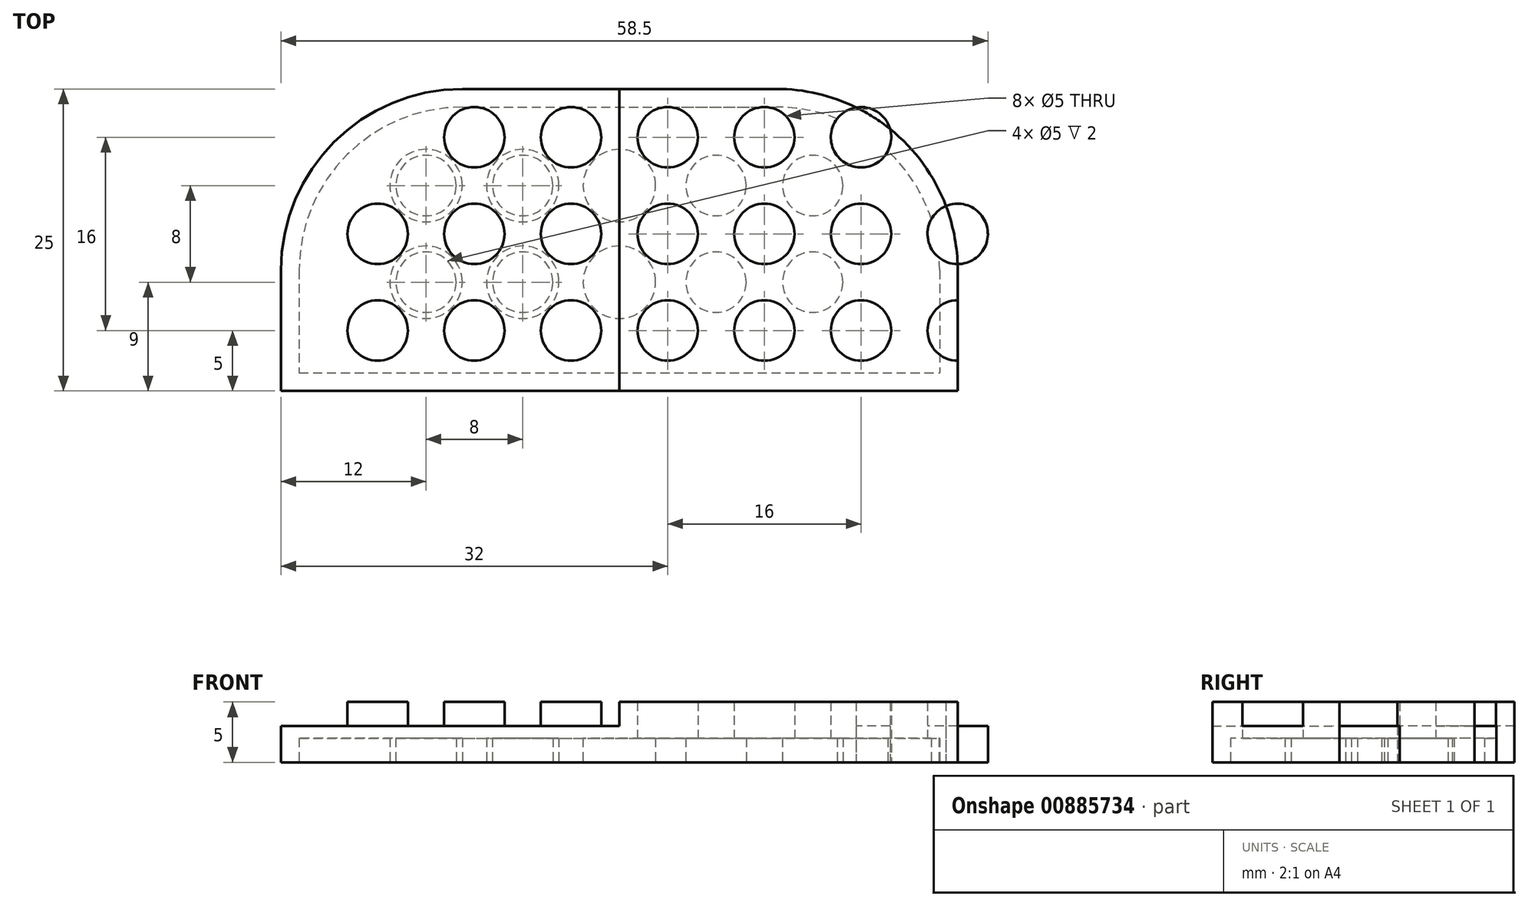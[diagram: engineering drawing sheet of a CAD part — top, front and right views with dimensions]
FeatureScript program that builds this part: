
annotation { "Feature Type Name" : "Feature", "Feature Type Description" : "" }
export const myFeature = defineFeature(function(context is Context, id is Id, definition is map)
    precondition{}
    {
        {
            var Q0;
            Q0=qCreatedBy(makeId("Top.planeOp"),FACE);
            var sketch = newSketch(context, id + "F0", { "sketchPlane" : qUnion([Q0])});
            skLineSegment(sketch, "E0.bottom", {"start": v(0, 0) * mm, "end": v(-28, 0) * mm});
            skLineSegment(sketch, "E0.top", {"start": v(0, 25) * mm, "end": v(-13, 25) * mm});
            skLineSegment(sketch, "E0.left", {"start": v(0, 0) * mm, "end": v(0, 25) * mm});
            skLineSegment(sketch, "E0.right", {"start": v(-28, 0) * mm, "end": v(-28, 10) * mm});
            skPoint(sketch, "E1.visualSharp", {"position": v(-28, 25) * mm});
            skArc(sketch, "E1.filletArc", {"start": v(-13, 25) * mm, "mid": v(-23.6, 20.6) * mm, "end": v(-28, 10) * mm});
            skLineSegment(sketch, "E2.MirrorCS", {"start": v(0, 25) * mm, "end": v(13, 25) * mm});
            skArc(sketch, "E3.MirrorCS", {"start": v(13, 25) * mm, "mid": v(23.6, 20.6) * mm, "end": v(28, 10) * mm});
            skLineSegment(sketch, "E4.MirrorCS", {"start": v(28, 0) * mm, "end": v(28, 10) * mm});
            skLineSegment(sketch, "E5.MirrorCS", {"start": v(0, 0) * mm, "end": v(28, 0) * mm});
            skCircle(sketch, "E6", {"center": v(-20, 5) * mm, "radius": 2.5 * mm});
            skCircle(sketch, "E7", {"center": v(-12, 5) * mm, "radius": 2.5 * mm});
            skCircle(sketch, "E8", {"center": v(-4, 5) * mm, "radius": 2.5 * mm});
            skCircle(sketch, "E9.MirrorC", {"center": v(4, 5) * mm, "radius": 2.5 * mm});
            skCircle(sketch, "E10.MirrorC", {"center": v(12, 5) * mm, "radius": 2.5 * mm});
            skCircle(sketch, "E11.MirrorC", {"center": v(20, 5) * mm, "radius": 2.5 * mm});
            skCircle(sketch, "E12", {"center": v(-20, 13) * mm, "radius": 2.5 * mm});
            skCircle(sketch, "E13", {"center": v(-12, 13) * mm, "radius": 2.5 * mm});
            skCircle(sketch, "E14", {"center": v(-4, 13) * mm, "radius": 2.5 * mm});
            skCircle(sketch, "E15", {"center": v(-12, 21) * mm, "radius": 2.5 * mm});
            skCircle(sketch, "E16", {"center": v(-4, 21) * mm, "radius": 2.5 * mm});
            skCircle(sketch, "E17", {"center": v(-20, 21) * mm, "radius": 2.5 * mm});
            skCircle(sketch, "E18.MirrorC", {"center": v(4, 21) * mm, "radius": 2.5 * mm});
            skCircle(sketch, "E19.MirrorC", {"center": v(12, 21) * mm, "radius": 2.5 * mm});
            skCircle(sketch, "E20.MirrorC", {"center": v(20, 21) * mm, "radius": 2.5 * mm});
            skCircle(sketch, "E21.MirrorC", {"center": v(20, 13) * mm, "radius": 2.5 * mm});
            skCircle(sketch, "E22.MirrorC", {"center": v(12, 13) * mm, "radius": 2.5 * mm});
            skCircle(sketch, "E23.MirrorC", {"center": v(4, 13) * mm, "radius": 2.5 * mm});
            skCircle(sketch, "E24", {"center": v(28, 13) * mm, "radius": 2.5 * mm});
            skCircle(sketch, "E25", {"center": v(28, 5) * mm, "radius": 2.5 * mm});
            skCircle(sketch, "E26.MirrorC", {"center": v(-28, 13) * mm, "radius": 2.5 * mm});
            skCircle(sketch, "E27.MirrorC", {"center": v(-28, 5) * mm, "radius": 2.5 * mm});
            skCircle(sketch, "E28", {"center": v(-28, 21) * mm, "radius": 2.5 * mm});
            skCircle(sketch, "E29.MirrorC", {"center": v(28, 21) * mm, "radius": 2.5 * mm});
            skSolve(sketch);
        }
        {
            var Q0;
            {var subQ12=sQuery(id+"F0.wireOp",EDGE,"E0.bottom");Q0=makeQuery(id+"F0.imprint","IMPRINT",FACE,{"disambiguationData":[TD([[makeQuery(id+"F0.imprint","IMPRINT",EDGE,{"derivedFrom":subQ12}),-1.0]])]});}
            var Q1;
            {var subQ0=sQuery(id+"F0.wireOp",EDGE,"E17");var subQ1=sQuery(id+"F0.wireOp",EDGE,"E1.filletArc");var subQ2=makeQuery(id+"F0.imprint","INTERSECT",VERTEX,{"disambiguationData":[OD(0.0)],"derivedFrom":[subQ1,subQ0]});Q1=makeQuery(id+"F0.imprint","IMPRINT",FACE,{"disambiguationData":[TD([[makeQuery(id+"F0.imprint","IMPRINT",EDGE,{"disambiguationData":[TD([[subQ2,-1.0]])],"derivedFrom":subQ1}),1.0]])]});}
            var Q2;
            {var subQ10=sQuery(id+"F0.wireOp",EDGE,"E2.MirrorCS");Q2=makeQuery(id+"F0.imprint","IMPRINT",FACE,{"disambiguationData":[TD([[makeQuery(id+"F0.imprint","IMPRINT",EDGE,{"derivedFrom":subQ10}),-1.0]])]});}
            var Q3;
            {var subQ0=sQuery(id+"F0.wireOp",EDGE,"E20.MirrorC");var subQ1=sQuery(id+"F0.wireOp",EDGE,"E3.MirrorCS");var subQ2=makeQuery(id+"F0.imprint","INTERSECT",VERTEX,{"disambiguationData":[OD(0.0)],"derivedFrom":[subQ1,subQ0]});Q3=makeQuery(id+"F0.imprint","IMPRINT",FACE,{"disambiguationData":[TD([[makeQuery(id+"F0.imprint","IMPRINT",EDGE,{"disambiguationData":[TD([[subQ2,-1.0]])],"derivedFrom":subQ1}),-1.0]])]});}
            var Q4;
            {var subQ0=sQuery(id+"F0.wireOp",EDGE,"E26.MirrorC");var subQ1=sQuery(id+"F0.wireOp",EDGE,"E1.filletArc");var subQ2=makeQuery(id+"F0.imprint","INTERSECT",VERTEX,{"disambiguationData":[OD(0.0)],"derivedFrom":[subQ1,subQ0]});Q4=makeQuery(id+"F0.imprint","IMPRINT",FACE,{"disambiguationData":[TD([[makeQuery(id+"F0.imprint","IMPRINT",EDGE,{"disambiguationData":[TD([[subQ2,-1.0]])],"derivedFrom":subQ1}),1.0]])]});}
            var Q5;
            {var subQ0=sQuery(id+"F0.wireOp",EDGE,"E27.MirrorC");var subQ1=sQuery(id+"F0.wireOp",EDGE,"E0.right");var subQ2=makeQuery(id+"F0.imprint","INTERSECT",VERTEX,{"disambiguationData":[OD(0.0)],"derivedFrom":[subQ1,subQ0]});Q5=makeQuery(id+"F0.imprint","IMPRINT",FACE,{"disambiguationData":[TD([[makeQuery(id+"F0.imprint","IMPRINT",EDGE,{"disambiguationData":[TD([[subQ2,-1.0]])],"derivedFrom":subQ1}),-1.0]])]});}
            var Q6;
            {var subQ0=sQuery(id+"F0.wireOp",EDGE,"E25");var subQ1=sQuery(id+"F0.wireOp",EDGE,"E4.MirrorCS");var subQ2=makeQuery(id+"F0.imprint","INTERSECT",VERTEX,{"disambiguationData":[OD(0.0)],"derivedFrom":[subQ1,subQ0]});Q6=makeQuery(id+"F0.imprint","IMPRINT",FACE,{"disambiguationData":[TD([[makeQuery(id+"F0.imprint","IMPRINT",EDGE,{"disambiguationData":[TD([[subQ2,-1.0]])],"derivedFrom":subQ1}),1.0]])]});}
            var Q7;
            {var subQ0=sQuery(id+"F0.wireOp",EDGE,"E24");var subQ1=sQuery(id+"F0.wireOp",EDGE,"E3.MirrorCS");var subQ2=makeQuery(id+"F0.imprint","INTERSECT",VERTEX,{"disambiguationData":[OD(0.0)],"derivedFrom":[subQ1,subQ0]});Q7=makeQuery(id+"F0.imprint","IMPRINT",FACE,{"disambiguationData":[TD([[makeQuery(id+"F0.imprint","IMPRINT",EDGE,{"disambiguationData":[TD([[subQ2,-1.0]])],"derivedFrom":subQ1}),-1.0]])]});}
            extrude(context, id + "F1", {"entities" : qUnion([Q0, Q1, Q2, Q3, Q4, Q5, Q6, Q7]), "depth" : 3 * mm, "offsetDistance" : 25 * mm});
        }
        {
            var Q0;
            Q0=makeQuery(id+"F0.imprint","IMPRINT",FACE,{"disambiguationData":[TD([[makeQuery(id+"F0.imprint","IMPRINT",EDGE,{"derivedFrom":sQuery(id+"F0.wireOp",EDGE,"E12")}),1.0]])]});
            var Q1;
            Q1=makeQuery(id+"F0.imprint","IMPRINT",FACE,{"disambiguationData":[TD([[makeQuery(id+"F0.imprint","IMPRINT",EDGE,{"derivedFrom":sQuery(id+"F0.wireOp",EDGE,"E6")}),1.0]])]});
            var Q2;
            Q2=makeQuery(id+"F0.imprint","IMPRINT",FACE,{"disambiguationData":[TD([[makeQuery(id+"F0.imprint","IMPRINT",EDGE,{"derivedFrom":sQuery(id+"F0.wireOp",EDGE,"E7")}),1.0]])]});
            var Q3;
            Q3=makeQuery(id+"F0.imprint","IMPRINT",FACE,{"disambiguationData":[TD([[makeQuery(id+"F0.imprint","IMPRINT",EDGE,{"derivedFrom":sQuery(id+"F0.wireOp",EDGE,"E13")}),1.0]])]});
            var Q4;
            Q4=makeQuery(id+"F0.imprint","IMPRINT",FACE,{"disambiguationData":[TD([[makeQuery(id+"F0.imprint","IMPRINT",EDGE,{"derivedFrom":sQuery(id+"F0.wireOp",EDGE,"E15")}),1.0]])]});
            var Q5;
            Q5=makeQuery(id+"F0.imprint","IMPRINT",FACE,{"disambiguationData":[TD([[makeQuery(id+"F0.imprint","IMPRINT",EDGE,{"derivedFrom":sQuery(id+"F0.wireOp",EDGE,"E16")}),1.0]])]});
            var Q6;
            Q6=makeQuery(id+"F0.imprint","IMPRINT",FACE,{"disambiguationData":[TD([[makeQuery(id+"F0.imprint","IMPRINT",EDGE,{"derivedFrom":sQuery(id+"F0.wireOp",EDGE,"E14")}),1.0]])]});
            var Q7;
            Q7=makeQuery(id+"F0.imprint","IMPRINT",FACE,{"disambiguationData":[TD([[makeQuery(id+"F0.imprint","IMPRINT",EDGE,{"derivedFrom":sQuery(id+"F0.wireOp",EDGE,"E8")}),1.0]])]});
            var Q8;
            Q8=makeQuery(id+"F0.imprint","IMPRINT",FACE,{"disambiguationData":[TD([[makeQuery(id+"F0.imprint","IMPRINT",EDGE,{"derivedFrom":sQuery(id+"F0.wireOp",EDGE,"E23.MirrorC")}),-1.0]])]});
            var Q9;
            Q9=makeQuery(id+"F0.imprint","IMPRINT",FACE,{"disambiguationData":[TD([[makeQuery(id+"F0.imprint","IMPRINT",EDGE,{"derivedFrom":sQuery(id+"F0.wireOp",EDGE,"E18.MirrorC")}),-1.0]])]});
            var Q10;
            Q10=makeQuery(id+"F0.imprint","IMPRINT",FACE,{"disambiguationData":[TD([[makeQuery(id+"F0.imprint","IMPRINT",EDGE,{"derivedFrom":sQuery(id+"F0.wireOp",EDGE,"E9.MirrorC")}),-1.0]])]});
            var Q11;
            Q11=makeQuery(id+"F0.imprint","IMPRINT",FACE,{"disambiguationData":[TD([[makeQuery(id+"F0.imprint","IMPRINT",EDGE,{"derivedFrom":sQuery(id+"F0.wireOp",EDGE,"E10.MirrorC")}),-1.0]])]});
            var Q12;
            Q12=makeQuery(id+"F0.imprint","IMPRINT",FACE,{"disambiguationData":[TD([[makeQuery(id+"F0.imprint","IMPRINT",EDGE,{"derivedFrom":sQuery(id+"F0.wireOp",EDGE,"E22.MirrorC")}),-1.0]])]});
            var Q13;
            Q13=makeQuery(id+"F0.imprint","IMPRINT",FACE,{"disambiguationData":[TD([[makeQuery(id+"F0.imprint","IMPRINT",EDGE,{"derivedFrom":sQuery(id+"F0.wireOp",EDGE,"E19.MirrorC")}),-1.0]])]});
            var Q14;
            Q14=makeQuery(id+"F0.imprint","IMPRINT",FACE,{"disambiguationData":[TD([[makeQuery(id+"F0.imprint","IMPRINT",EDGE,{"derivedFrom":sQuery(id+"F0.wireOp",EDGE,"E21.MirrorC")}),-1.0]])]});
            var Q15;
            Q15=makeQuery(id+"F0.imprint","IMPRINT",FACE,{"disambiguationData":[TD([[makeQuery(id+"F0.imprint","IMPRINT",EDGE,{"derivedFrom":sQuery(id+"F0.wireOp",EDGE,"E11.MirrorC")}),-1.0]])]});
            extrude(context, id + "F2", {"entities" : qUnion([Q0, Q1, Q2, Q3, Q4, Q5, Q6, Q7, Q8, Q9, Q10, Q11, Q12, Q13, Q14, Q15]), "operationType" : NewBodyOperationType.ADD, "depth" : 5 * mm, "offsetDistance" : 25 * mm});
        }
        {
            var Q0;
            Q0=qCreatedBy(makeId("Top.planeOp"),FACE);
            var sketch = newSketch(context, id + "F3", { "sketchPlane" : qUnion([Q0])});
            skCircle(sketch, "E30", {"center": v(-16, 9) * mm, "radius": 2.5 * mm});
            skCircle(sketch, "E31", {"center": v(-8, 9) * mm, "radius": 2.5 * mm});
            skCircle(sketch, "E32", {"center": v(0, 9) * mm, "radius": 2.5 * mm});
            skCircle(sketch, "E33", {"center": v(0, 17) * mm, "radius": 2.5 * mm});
            skCircle(sketch, "E34", {"center": v(-8, 17) * mm, "radius": 2.5 * mm});
            skCircle(sketch, "E35", {"center": v(-16, 17) * mm, "radius": 2.5 * mm});
            skLineSegment(sketch, "E36", {"start": v(0, 23.5) * mm, "end": v(-13, 23.5) * mm});
            skLineSegment(sketch, "E37", {"start": v(-26.5, 10) * mm, "end": v(-26.5, 1.5) * mm});
            skLineSegment(sketch, "E38", {"start": v(-26.5, 1.5) * mm, "end": v(0, 1.5) * mm});
            skPoint(sketch, "E39.visualSharp", {"position": v(-26.5, 23.5) * mm});
            skArc(sketch, "E39.filletArc", {"start": v(-13, 23.5) * mm, "mid": v(-22.55, 19.55) * mm, "end": v(-26.5, 10) * mm});
            skCircle(sketch, "E40", {"center": v(0, 17) * mm, "radius": 3 * mm});
            skCircle(sketch, "E41", {"center": v(-8, 17) * mm, "radius": 3 * mm});
            skCircle(sketch, "E42", {"center": v(-16, 17) * mm, "radius": 3 * mm});
            skCircle(sketch, "E43", {"center": v(-16, 9) * mm, "radius": 3 * mm});
            skCircle(sketch, "E44", {"center": v(-8, 9) * mm, "radius": 3 * mm});
            skCircle(sketch, "E45", {"center": v(0, 9) * mm, "radius": 3 * mm});
            skLineSegment(sketch, "E46", {"start": v(0, 23.5) * mm, "end": v(0, 25) * mm});
            skLineSegment(sketch, "E47", {"start": v(0, 25) * mm, "end": v(-13, 25) * mm});
            skArc(sketch, "E48", {"start": v(-13, 25) * mm, "mid": v(-23.6, 20.6) * mm, "end": v(-28, 10) * mm});
            skLineSegment(sketch, "E49", {"start": v(-28, 10) * mm, "end": v(-28, 0) * mm});
            skLineSegment(sketch, "E50", {"start": v(-28, 0) * mm, "end": v(0, 0) * mm});
            skLineSegment(sketch, "E51", {"start": v(0, 0) * mm, "end": v(0, 1.5) * mm});
            skLineSegment(sketch, "E52", {"start": v(-18, 22.54) * mm, "end": v(-19.15, 23.68) * mm});
            skLineSegment(sketch, "E53", {"start": v(-22.31, 19.78) * mm, "end": v(-23.37, 20.84) * mm});
            skLineSegment(sketch, "E54.MirrorCS", {"start": v(26.5, 1.5) * mm, "end": v(0, 1.5) * mm});
            skLineSegment(sketch, "E55.MirrorCS", {"start": v(28, 0) * mm, "end": v(0, 0) * mm});
            skLineSegment(sketch, "E56.MirrorCS", {"start": v(26.5, 10) * mm, "end": v(26.5, 1.5) * mm});
            skArc(sketch, "E57.MirrorCS", {"start": v(13, 25) * mm, "mid": v(23.6, 20.6) * mm, "end": v(28, 10) * mm});
            skLineSegment(sketch, "E58.MirrorCS", {"start": v(0, 25) * mm, "end": v(13, 25) * mm});
            skLineSegment(sketch, "E59.MirrorCS", {"start": v(0, 23.5) * mm, "end": v(13, 23.5) * mm});
            skArc(sketch, "E60.MirrorCS", {"start": v(13, 23.5) * mm, "mid": v(22.55, 19.55) * mm, "end": v(26.5, 10) * mm});
            skLineSegment(sketch, "E61.MirrorCS", {"start": v(28, 10) * mm, "end": v(28, 0) * mm});
            skCircle(sketch, "E62.MirrorC", {"center": v(8, 17) * mm, "radius": 2.5 * mm});
            skCircle(sketch, "E63.MirrorC", {"center": v(8, 17) * mm, "radius": 3 * mm});
            skCircle(sketch, "E64.MirrorC", {"center": v(8, 9) * mm, "radius": 3 * mm});
            skCircle(sketch, "E65.MirrorC", {"center": v(8, 9) * mm, "radius": 2.5 * mm});
            skCircle(sketch, "E66.MirrorC", {"center": v(16, 9) * mm, "radius": 2.5 * mm});
            skCircle(sketch, "E67.MirrorC", {"center": v(16, 9) * mm, "radius": 3 * mm});
            skCircle(sketch, "E68.MirrorC", {"center": v(16, 17) * mm, "radius": 2.5 * mm});
            skCircle(sketch, "E69.MirrorC", {"center": v(16, 17) * mm, "radius": 3 * mm});
            skLineSegment(sketch, "E70.MirrorCS", {"start": v(18, 22.54) * mm, "end": v(19.15, 23.68) * mm});
            skLineSegment(sketch, "E71.MirrorCS", {"start": v(22.31, 19.78) * mm, "end": v(23.37, 20.84) * mm});
            skCircle(sketch, "E72", {"center": v(24, 9) * mm, "radius": 2.5 * mm});
            skCircle(sketch, "E73", {"center": v(24, 9) * mm, "radius": 3 * mm});
            skSolve(sketch);
        }
        {
            var Q0;
            Q0=makeQuery(id+"F3.imprint","IMPRINT",FACE,{"disambiguationData":[TD([[makeQuery(id+"F3.imprint","IMPRINT",EDGE,{"derivedFrom":sQuery(id+"F3.wireOp",EDGE,"E66.MirrorC")}),-1.0]])]});
            var Q1;
            Q1=makeQuery(id+"F3.imprint","IMPRINT",FACE,{"disambiguationData":[TD([[makeQuery(id+"F3.imprint","IMPRINT",EDGE,{"derivedFrom":sQuery(id+"F3.wireOp",EDGE,"E65.MirrorC")}),-1.0]])]});
            var Q2;
            Q2=makeQuery(id+"F3.imprint","IMPRINT",FACE,{"disambiguationData":[TD([[makeQuery(id+"F3.imprint","IMPRINT",EDGE,{"derivedFrom":sQuery(id+"F3.wireOp",EDGE,"E62.MirrorC")}),-1.0]])]});
            var Q3;
            Q3=makeQuery(id+"F3.imprint","IMPRINT",FACE,{"disambiguationData":[TD([[makeQuery(id+"F3.imprint","IMPRINT",EDGE,{"derivedFrom":sQuery(id+"F3.wireOp",EDGE,"E68.MirrorC")}),-1.0]])]});
            var Q4;
            {var subQ9=sQuery(id+"F3.wireOp",EDGE,"E36");Q4=makeQuery(id+"F3.imprint","IMPRINT",FACE,{"disambiguationData":[TD([[makeQuery(id+"F3.imprint","IMPRINT",EDGE,{"derivedFrom":subQ9}),1.0]])]});}
            var Q5;
            Q5=makeQuery(id+"F3.imprint","IMPRINT",FACE,{"disambiguationData":[TD([[makeQuery(id+"F3.imprint","IMPRINT",EDGE,{"derivedFrom":sQuery(id+"F3.wireOp",EDGE,"E32")}),-1.0]])]});
            var Q6;
            Q6=makeQuery(id+"F3.imprint","IMPRINT",FACE,{"disambiguationData":[TD([[makeQuery(id+"F3.imprint","IMPRINT",EDGE,{"derivedFrom":sQuery(id+"F3.wireOp",EDGE,"E31")}),1.0]])]});
            var Q7;
            Q7=makeQuery(id+"F3.imprint","IMPRINT",FACE,{"disambiguationData":[TD([[makeQuery(id+"F3.imprint","IMPRINT",EDGE,{"derivedFrom":sQuery(id+"F3.wireOp",EDGE,"E30")}),1.0]])]});
            var Q8;
            Q8=makeQuery(id+"F3.imprint","IMPRINT",FACE,{"disambiguationData":[TD([[makeQuery(id+"F3.imprint","IMPRINT",EDGE,{"derivedFrom":sQuery(id+"F3.wireOp",EDGE,"E35")}),1.0]])]});
            var Q9;
            Q9=makeQuery(id+"F3.imprint","IMPRINT",FACE,{"disambiguationData":[TD([[makeQuery(id+"F3.imprint","IMPRINT",EDGE,{"derivedFrom":sQuery(id+"F3.wireOp",EDGE,"E34")}),1.0]])]});
            var Q10;
            Q10=makeQuery(id+"F3.imprint","IMPRINT",FACE,{"disambiguationData":[TD([[makeQuery(id+"F3.imprint","IMPRINT",EDGE,{"derivedFrom":sQuery(id+"F3.wireOp",EDGE,"E33")}),-1.0]])]});
            var Q11;
            Q11=makeQuery(id+"F3.imprint","IMPRINT",FACE,{"disambiguationData":[TD([[makeQuery(id+"F3.imprint","IMPRINT",EDGE,{"derivedFrom":sQuery(id+"F3.wireOp",EDGE,"E72")}),1.0]])]});
            var Q12;
            {var subQ5=sQuery(id+"F3.wireOp",EDGE,"E72");Q12=makeQuery(id+"F3.imprint","IMPRINT",FACE,{"disambiguationData":[TD([[makeQuery(id+"F3.imprint","IMPRINT",EDGE,{"derivedFrom":subQ5}),-1.0]])]});}
            extrude(context, id + "F4", {"entities" : qUnion([Q0, Q1, Q2, Q3, Q4, Q5, Q6, Q7, Q8, Q9, Q10, Q11, Q12]), "operationType" : NewBodyOperationType.REMOVE, "depth" : 2 * mm, "offsetDistance" : 25 * mm});
        }
    });
